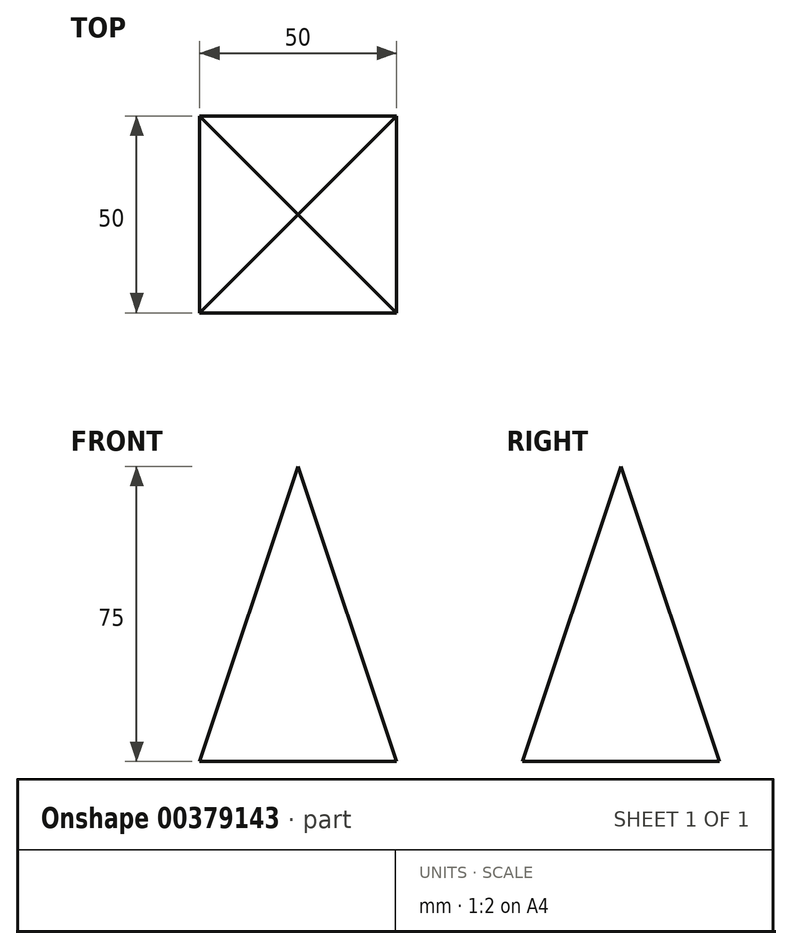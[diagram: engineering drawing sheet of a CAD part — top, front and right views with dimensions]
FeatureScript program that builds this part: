
annotation { "Feature Type Name" : "Feature", "Feature Type Description" : "" }
export const myFeature = defineFeature(function(context is Context, id is Id, definition is map)
    precondition{}
    {
        {
            var Q0;
            Q0=qCreatedBy(makeId("Top.planeOp"),FACE);
            var sketch = newSketch(context, id + "F0", { "sketchPlane" : qUnion([Q0])});
            skLineSegment(sketch, "E0.bottom", {"start": v(-25, 25) * mm, "end": v(25, 25) * mm});
            skLineSegment(sketch, "E0.top", {"start": v(-25, -25) * mm, "end": v(25, -25) * mm});
            skLineSegment(sketch, "E0.left", {"start": v(-25, 25) * mm, "end": v(-25, -25) * mm});
            skLineSegment(sketch, "E0.right", {"start": v(25, 25) * mm, "end": v(25, -25) * mm});
            skPoint(sketch, "E0.middle", {"position": v(0, 0) * mm});
            skSolve(sketch);
        }
        {
            var Q0;
            Q0=qCreatedBy(makeId("Front.planeOp"),FACE);
            var sketch = newSketch(context, id + "F1", { "sketchPlane" : qUnion([Q0])});
            skLineSegment(sketch, "E1", {"start": v(0, 0) * mm, "end": v(0, 75) * mm});
            skSolve(sketch);
        }
        {
            var Q0;
            Q0=makeQuery(id+"F0.imprint","IMPRINT",FACE,{"disambiguationData":[TD([[makeQuery(id+"F0.imprint","IMPRINT",EDGE,{"derivedFrom":sQuery(id+"F0.wireOp",EDGE,"E0.bottom")}),-1.0]])]});
            var Q1;
            Q1=sQuery(id+"F1.wireOp",VERTEX,"E1.end");
            loft(context, id + "F2", {"sheetProfilesArray" : [{ "sheetProfileEntities" : qUnion([Q0]) }, { "sheetProfileEntities" : qUnion([Q1]) }]});
        }
    });
